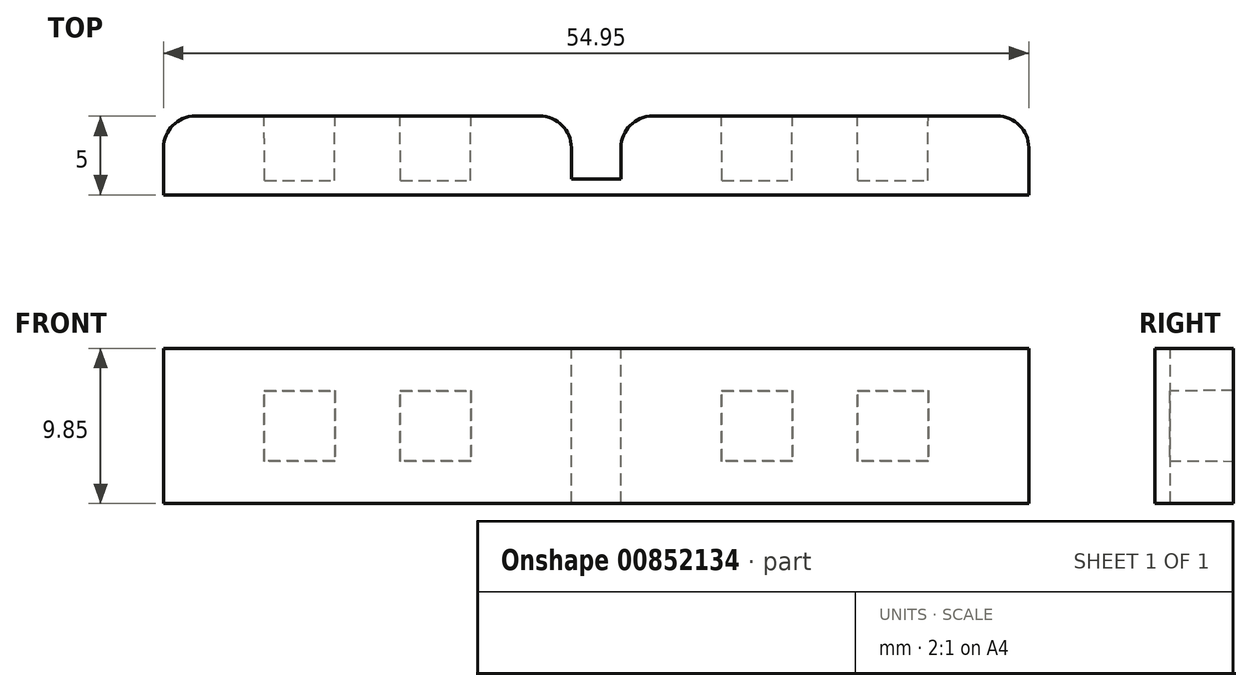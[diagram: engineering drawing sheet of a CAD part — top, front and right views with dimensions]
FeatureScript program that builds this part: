
annotation { "Feature Type Name" : "Feature", "Feature Type Description" : "" }
export const myFeature = defineFeature(function(context is Context, id is Id, definition is map)
    precondition{}
    {
        {
            var Q0;
            Q0=qCreatedBy(makeId("Front.planeOp"),FACE);
            var sketch = newSketch(context, id + "F0", { "sketchPlane" : qUnion([Q0])});
            skLineSegment(sketch, "E0.bottom", {"start": v(-15.5, 0) * mm, "end": v(-41.4, 0) * mm});
            skLineSegment(sketch, "E0.top", {"start": v(-15.5, 9.85) * mm, "end": v(-41.4, 9.85) * mm});
            skLineSegment(sketch, "E0.left", {"start": v(-15.5, 0) * mm, "end": v(-15.5, 9.85) * mm});
            skLineSegment(sketch, "E0.right", {"start": v(-41.4, 0) * mm, "end": v(-41.4, 9.85) * mm});
            skLineSegment(sketch, "E1.bottom", {"start": v(-12.35, 0) * mm, "end": v(13.55, 0) * mm});
            skLineSegment(sketch, "E1.top", {"start": v(-12.35, 9.85) * mm, "end": v(13.55, 9.85) * mm});
            skLineSegment(sketch, "E1.left", {"start": v(-12.35, 0) * mm, "end": v(-12.35, 9.85) * mm});
            skLineSegment(sketch, "E1.right", {"start": v(13.55, 0) * mm, "end": v(13.55, 9.85) * mm});
            skLineSegment(sketch, "E2", {"start": v(-15.5, 9.85) * mm, "end": v(-12.35, 9.85) * mm});
            skLineSegment(sketch, "E3", {"start": v(-15.5, 0) * mm, "end": v(-12.35, 0) * mm});
            skLineSegment(sketch, "E4.bottom", {"start": v(7.17, 7.17) * mm, "end": v(2.67, 7.17) * mm});
            skLineSegment(sketch, "E4.top", {"start": v(7.17, 2.67) * mm, "end": v(2.67, 2.67) * mm});
            skLineSegment(sketch, "E4.left", {"start": v(7.17, 7.18) * mm, "end": v(7.17, 2.67) * mm});
            skLineSegment(sketch, "E4.right", {"start": v(2.67, 7.17) * mm, "end": v(2.67, 2.67) * mm});
            skPoint(sketch, "E4.middle", {"position": v(4.92, 4.92) * mm});
            skLineSegment(sketch, "E5.bottom", {"start": v(-1.46, 7.17) * mm, "end": v(-5.96, 7.17) * mm});
            skLineSegment(sketch, "E5.top", {"start": v(-1.46, 2.67) * mm, "end": v(-5.96, 2.67) * mm});
            skLineSegment(sketch, "E5.left", {"start": v(-1.46, 7.17) * mm, "end": v(-1.46, 2.67) * mm});
            skLineSegment(sketch, "E5.right", {"start": v(-5.96, 7.17) * mm, "end": v(-5.96, 2.67) * mm});
            skPoint(sketch, "E5.middle", {"position": v(-3.71, 4.92) * mm});
            skLineSegment(sketch, "E6.bottom", {"start": v(-21.88, 7.17) * mm, "end": v(-26.38, 7.17) * mm});
            skLineSegment(sketch, "E6.top", {"start": v(-21.88, 2.67) * mm, "end": v(-26.38, 2.67) * mm});
            skLineSegment(sketch, "E6.left", {"start": v(-21.88, 7.17) * mm, "end": v(-21.88, 2.67) * mm});
            skLineSegment(sketch, "E6.right", {"start": v(-26.38, 7.17) * mm, "end": v(-26.38, 2.67) * mm});
            skPoint(sketch, "E6.middle", {"position": v(-24.13, 4.92) * mm});
            skLineSegment(sketch, "E7.bottom", {"start": v(-30.51, 7.17) * mm, "end": v(-35.01, 7.17) * mm});
            skLineSegment(sketch, "E7.top", {"start": v(-30.51, 2.67) * mm, "end": v(-35.01, 2.67) * mm});
            skLineSegment(sketch, "E7.left", {"start": v(-30.51, 7.17) * mm, "end": v(-30.51, 2.67) * mm});
            skLineSegment(sketch, "E7.right", {"start": v(-35.01, 7.17) * mm, "end": v(-35.01, 2.67) * mm});
            skPoint(sketch, "E7.middle", {"position": v(-32.76, 4.92) * mm});
            skLineSegment(sketch, "E8", {"start": v(-41.4, 4.92) * mm, "end": v(13.55, 4.93) * mm, "construction": true});
            skLineSegment(sketch, "E9", {"start": v(-32.76, 4.92) * mm, "end": v(-32.76, 0) * mm, "construction": true});
            skLineSegment(sketch, "E10", {"start": v(-24.13, 4.92) * mm, "end": v(-24.13, 0) * mm, "construction": true});
            skLineSegment(sketch, "E11", {"start": v(-3.71, 4.92) * mm, "end": v(-3.71, 0) * mm, "construction": true});
            skLineSegment(sketch, "E12", {"start": v(4.92, 4.92) * mm, "end": v(4.92, 0) * mm, "construction": true});
            skSolve(sketch);
        }
        {
            var Q0;
            Q0=makeQuery(id+"F0.imprint","IMPRINT",FACE,{"disambiguationData":[TD([[makeQuery(id+"F0.imprint","IMPRINT",EDGE,{"derivedFrom":sQuery(id+"F0.wireOp",EDGE,"E0.bottom")}),-1.0]])]});
            var Q1;
            Q1=makeQuery(id+"F0.imprint","IMPRINT",FACE,{"disambiguationData":[TD([[makeQuery(id+"F0.imprint","IMPRINT",EDGE,{"derivedFrom":sQuery(id+"F0.wireOp",EDGE,"E1.bottom")}),1.0]])]});
            var Q2;
            Q2=makeQuery(id+"F0.imprint","IMPRINT",FACE,{"disambiguationData":[TD([[makeQuery(id+"F0.imprint","IMPRINT",EDGE,{"derivedFrom":sQuery(id+"F0.wireOp",EDGE,"E4.bottom")}),1.0]])]});
            var Q3;
            Q3=makeQuery(id+"F0.imprint","IMPRINT",FACE,{"disambiguationData":[TD([[makeQuery(id+"F0.imprint","IMPRINT",EDGE,{"derivedFrom":sQuery(id+"F0.wireOp",EDGE,"E5.bottom")}),1.0]])]});
            var Q4;
            Q4=makeQuery(id+"F0.imprint","IMPRINT",FACE,{"disambiguationData":[TD([[makeQuery(id+"F0.imprint","IMPRINT",EDGE,{"derivedFrom":sQuery(id+"F0.wireOp",EDGE,"E6.bottom")}),1.0]])]});
            var Q5;
            Q5=makeQuery(id+"F0.imprint","IMPRINT",FACE,{"disambiguationData":[TD([[makeQuery(id+"F0.imprint","IMPRINT",EDGE,{"derivedFrom":sQuery(id+"F0.wireOp",EDGE,"E7.bottom")}),1.0]])]});
            extrude(context, id + "F1", {"entities" : qUnion([Q0, Q1, Q2, Q3, Q4, Q5]), "depth" : 5 * mm, "offsetDistance" : 25 * mm});
        }
        {
            var Q0;
            Q0=makeQuery(id+"F0.imprint","IMPRINT",FACE,{"disambiguationData":[TD([[makeQuery(id+"F0.imprint","IMPRINT",EDGE,{"derivedFrom":sQuery(id+"F0.wireOp",EDGE,"E4.bottom")}),1.0]])]});
            var Q1;
            Q1=makeQuery(id+"F0.imprint","IMPRINT",FACE,{"disambiguationData":[TD([[makeQuery(id+"F0.imprint","IMPRINT",EDGE,{"derivedFrom":sQuery(id+"F0.wireOp",EDGE,"E5.bottom")}),1.0]])]});
            var Q2;
            Q2=makeQuery(id+"F0.imprint","IMPRINT",FACE,{"disambiguationData":[TD([[makeQuery(id+"F0.imprint","IMPRINT",EDGE,{"derivedFrom":sQuery(id+"F0.wireOp",EDGE,"E6.bottom")}),1.0]])]});
            var Q3;
            Q3=makeQuery(id+"F0.imprint","IMPRINT",FACE,{"disambiguationData":[TD([[makeQuery(id+"F0.imprint","IMPRINT",EDGE,{"derivedFrom":sQuery(id+"F0.wireOp",EDGE,"E7.bottom")}),1.0]])]});
            extrude(context, id + "F2", {"entities" : qUnion([Q0, Q1, Q2, Q3]), "operationType" : NewBodyOperationType.REMOVE, "depth" : 4.08 * mm, "offsetDistance" : 25 * mm, "hasDraft" : true, "draftAngle" : .5 * degree, "draftPullDirection" : true});
        }
        {
            var Q0;
            Q0=makeQuery(id+"F1.opExtrude","CAP_FACE",FACE,{"disambiguationData":[OSD([sQuery(id+"F0.wireOp",EDGE,"E0.bottom"),sQuery(id+"F0.wireOp",EDGE,"E0.top"),sQuery(id+"F0.wireOp",EDGE,"E0.left"),sQuery(id+"F0.wireOp",EDGE,"E0.right")])],"isStart":false});
            var sketch = newSketch(context, id + "F3", { "sketchPlane" : qUnion([Q0])});
            skLineSegment(sketch, "E13.0.0", {"start": v(-12.35, 9.85) * mm, "end": v(-12.35, 0) * mm});
            skLineSegment(sketch, "E13.0.1", {"start": v(-12.35, 0) * mm, "end": v(13.55, 0) * mm});
            skLineSegment(sketch, "E13.0.2", {"start": v(13.55, 0) * mm, "end": v(13.55, 9.85) * mm});
            skLineSegment(sketch, "E13.0.3", {"start": v(13.55, 9.85) * mm, "end": v(-12.35, 9.85) * mm});
            skLineSegment(sketch, "E14", {"start": v(-12.35, 0) * mm, "end": v(-15.5, 0) * mm});
            skLineSegment(sketch, "E15", {"start": v(-15.5, 9.85) * mm, "end": v(-12.35, 9.85) * mm});
            skSolve(sketch);
        }
        {
            var Q0;
            Q0=makeQuery(id+"F3.imprint","IMPRINT",FACE,{"disambiguationData":[TD([[makeQuery(id+"F3.imprint","IMPRINT",EDGE,{"derivedFrom":sQuery(id+"F3.wireOp",EDGE,"E13.0.0")}),-1.0]])]});
            extrude(context, id + "F4", {"entities" : qUnion([Q0]), "operationType" : NewBodyOperationType.ADD, "oppositeDirection" : true, "depth" : 1 * mm, "offsetDistance" : 25 * mm});
        }
        {
            var Q0;
            Q0=makeQuery(id+"F1.opExtrude","CAP_EDGE",EDGE,{"disambiguationData":[OSD([sQuery(id+"F0.wireOp",EDGE,"E1.left")])],"isStart":true});
            var Q1;
            Q1=makeQuery(id+"F1.opExtrude","CAP_EDGE",EDGE,{"disambiguationData":[OSD([sQuery(id+"F0.wireOp",EDGE,"E0.left")])],"isStart":true});
            var Q2;
            Q2=makeQuery(id+"F1.opExtrude","CAP_EDGE",EDGE,{"disambiguationData":[OSD([sQuery(id+"F0.wireOp",EDGE,"E1.right")])],"isStart":true});
            var Q3;
            Q3=makeQuery(id+"F1.opExtrude","CAP_EDGE",EDGE,{"disambiguationData":[OSD([sQuery(id+"F0.wireOp",EDGE,"E0.right")])],"isStart":true});
            fillet(context, id + "F5", {"entities" : qUnion([Q0, Q1, Q2, Q3]), "radius" : 2 * mm, "tangentPropagation" : true, "allowEdgeOverflow" : false});
        }
    });
